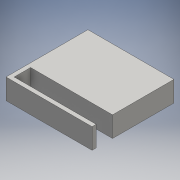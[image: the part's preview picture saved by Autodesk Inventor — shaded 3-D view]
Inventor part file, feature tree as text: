
AUTODESK INVENTOR PART (.ipt)
format: ipt  version: 2016 (Build 200138000, 138)  size: 129,536 bytes
history: native  units: mm
features: extrude x1, sketch x1
ambient origin geometry x8: Origin, YZ Plane, XZ Plane, XY Plane, X Axis, Y Axis, Z Axis, Center Point
bodies: Solid1 (feature_tree)
feature tree (2):
  extrude  "Extrusion1"  Depth=40.0mm
  sketch  "Sketch1"  dims[d0=42.0mm d1=40.0mm d2=30.0mm d3=10.0mm d4=0.0mm]
